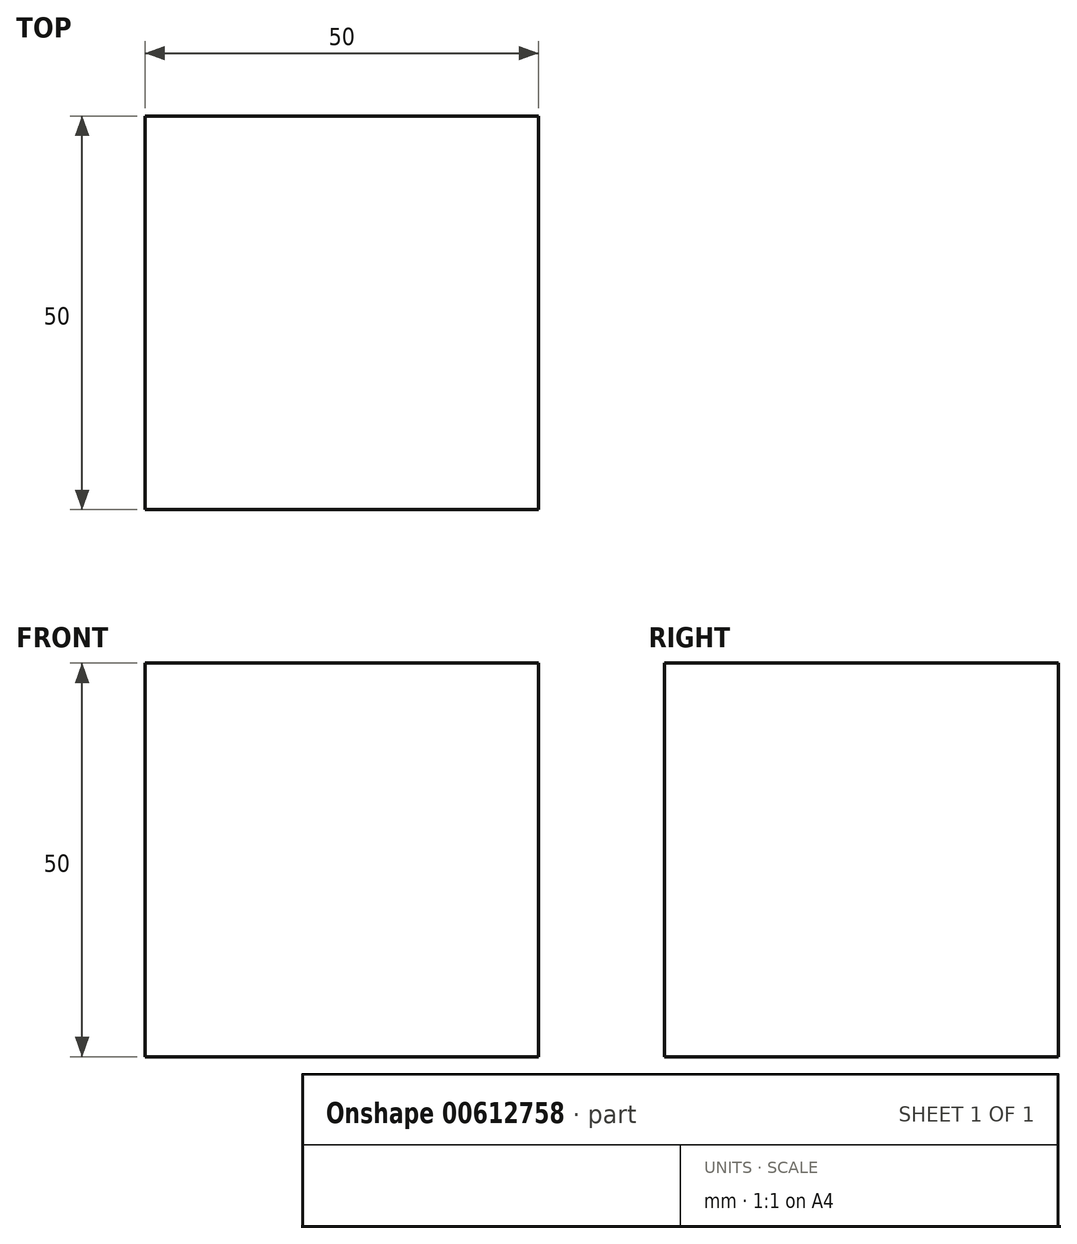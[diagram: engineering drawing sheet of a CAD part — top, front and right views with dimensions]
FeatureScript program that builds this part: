
annotation { "Feature Type Name" : "Feature", "Feature Type Description" : "" }
export const myFeature = defineFeature(function(context is Context, id is Id, definition is map)
    precondition{}
    {
        {
            var Q0;
            Q0=qCreatedBy(makeId("Top.planeOp"),FACE);
            var sketch = newSketch(context, id + "F0", { "sketchPlane" : qUnion([Q0])});
            skLineSegment(sketch, "E0.bottom", {"start": v(25, -25) * mm, "end": v(-25, -25) * mm});
            skLineSegment(sketch, "E0.top", {"start": v(25, 25) * mm, "end": v(-25, 25) * mm});
            skLineSegment(sketch, "E0.left", {"start": v(25, -25) * mm, "end": v(25, 25) * mm});
            skLineSegment(sketch, "E0.right", {"start": v(-25, -25) * mm, "end": v(-25, 25) * mm});
            skPoint(sketch, "E0.middle", {"position": v(0, 0) * mm});
            skSolve(sketch);
        }
        {
            var Q0;
            Q0 = qSketchRegion(id + "F0", true);
            extrude(context, id + "F1", {"entities" : qUnion([Q0]), "depth" : 50 * mm, "offsetDistance" : 25 * mm});
        }
    });
